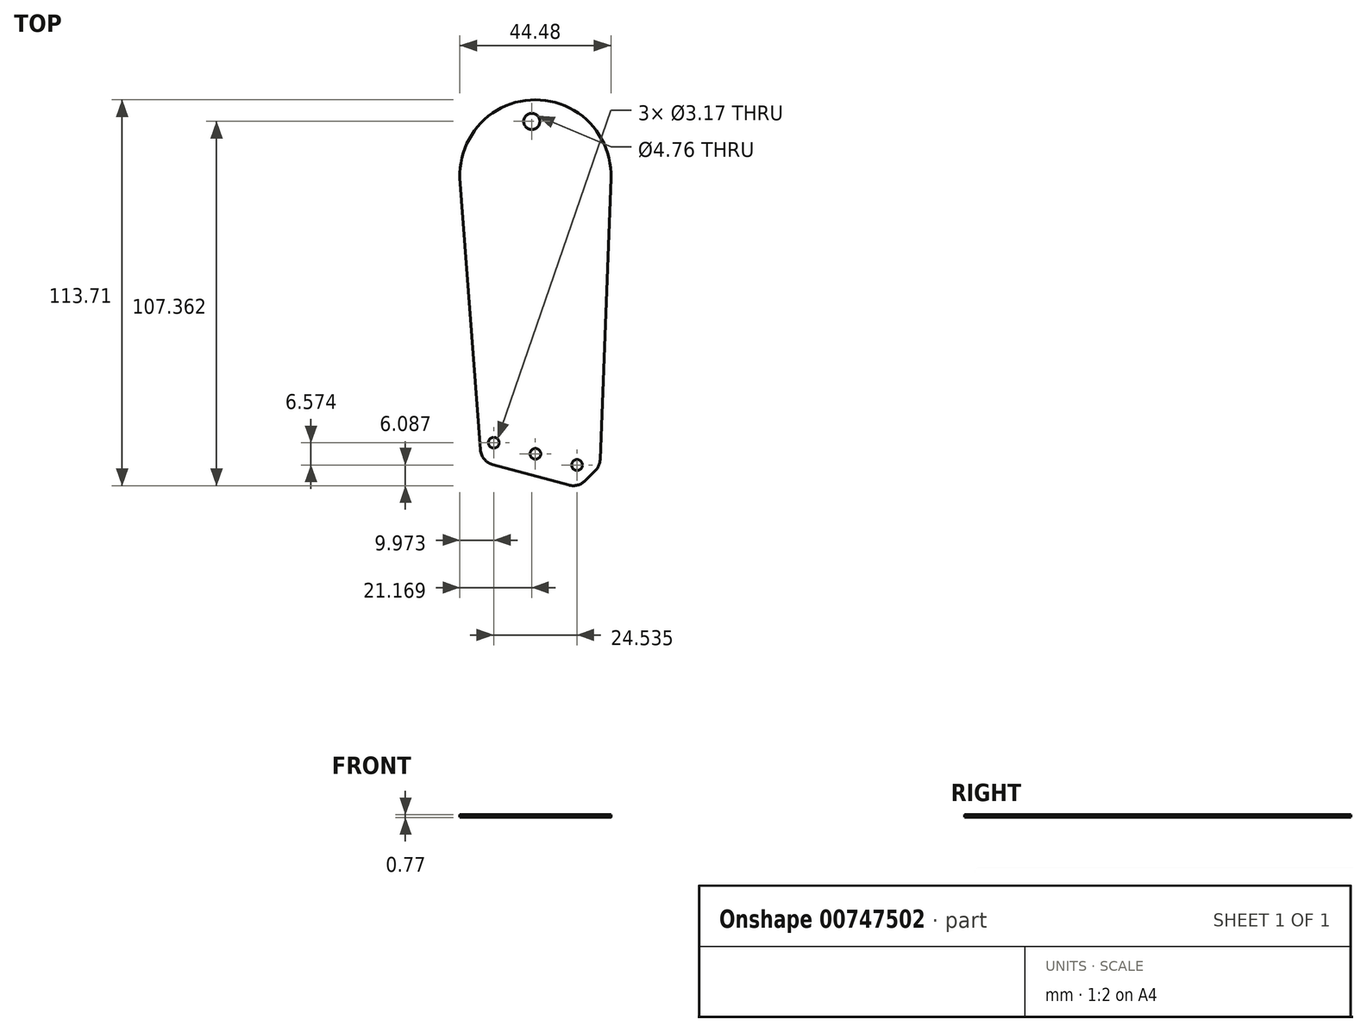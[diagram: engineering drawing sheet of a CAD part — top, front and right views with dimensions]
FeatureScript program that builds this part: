
annotation { "Feature Type Name" : "Feature", "Feature Type Description" : "" }
export const myFeature = defineFeature(function(context is Context, id is Id, definition is map)
    precondition{}
    {
        {
            var Q0;
            Q0=qCreatedBy(makeId("Right.planeOp"),FACE);
            var sketch = newSketch(context, id + "F0", { "sketchPlane" : qUnion([Q0])});
            skLineSegment(sketch, "E0", {"start": v(-73.39, -5.1) * mm, "end": v(-9.83, -5.1) * mm});
            skLineSegment(sketch, "E1", {"start": v(-9.83, -5.1) * mm, "end": v(40.91, -5.1) * mm});
            skPoint(sketch, "E2.visualSharp", {"position": v(-9.89, -5.1) * mm});
            skLineSegment(sketch, "E2.filletArc", {"start": v(-9.83, -5.1) * mm, "end": v(-9.83, -5.1) * mm});
            skLineSegment(sketch, "E3.0", {"start": v(-9.83, -5.87) * mm, "end": v(40.91, -5.87) * mm});
            skLineSegment(sketch, "E3.1", {"start": v(-9.83, -5.87) * mm, "end": v(-9.83, -5.87) * mm});
            skLineSegment(sketch, "E3.2", {"start": v(-73.39, -5.87) * mm, "end": v(-9.83, -5.87) * mm});
            skLineSegment(sketch, "E4", {"start": v(40.91, -5.87) * mm, "end": v(40.91, -5.1) * mm});
            skLineSegment(sketch, "E5", {"start": v(-73.39, -5.1) * mm, "end": v(-73.39, -5.87) * mm});
            skSolve(sketch);
        }
        {
            var Q0;
            Q0 = qSketchRegion(id + "F0", true);
            extrude(context, id + "F1", {"entities" : qUnion([Q0]), "endBound" : BoundingType.SYMMETRIC, "depth" : 101.6 * mm, "offsetDistance" : 25.4 * mm});
        }
        {
            var Q0;
            Q0=qCreatedBy(makeId("Top.planeOp"),FACE);
            var sketch = newSketch(context, id + "F2", { "sketchPlane" : qUnion([Q0])});
            skLineSegment(sketch, "E6", {"start": v(-20.03, 17.83) * mm, "end": v(-13.74, -65.73) * mm});
            skLineSegment(sketch, "E7", {"start": v(21.18, -67.04) * mm, "end": v(24.42, 17.83) * mm});
            skLineSegment(sketch, "E8", {"start": v(14.83, -73.39) * mm, "end": v(21.18, -67.04) * mm});
            skCircle(sketch, "E9", {"center": v(-10.5, -60.02) * mm, "radius": 1.59 * mm});
            skCircle(sketch, "E10", {"center": v(2.2, -63.43) * mm, "radius": 1.59 * mm});
            skCircle(sketch, "E11", {"center": v(14.9, -66.83) * mm, "radius": 1.59 * mm});
            skLineSegment(sketch, "E12.bottom", {"start": v(-71.62, 58.1) * mm, "end": v(69.87, 58.1) * mm});
            skLineSegment(sketch, "E12.top", {"start": v(-71.62, -139.59) * mm, "end": v(69.87, -139.59) * mm});
            skLineSegment(sketch, "E12.left", {"start": v(-71.62, 58.1) * mm, "end": v(-71.62, -139.59) * mm});
            skLineSegment(sketch, "E12.right", {"start": v(69.87, 58.1) * mm, "end": v(69.87, -139.59) * mm});
            skLineSegment(sketch, "E13", {"start": v(-10.5, -60.02) * mm, "end": v(14.9, -66.83) * mm});
            skLineSegment(sketch, "E14", {"start": v(-13.74, -65.73) * mm, "end": v(14.83, -73.39) * mm});
            skLineSegment(sketch, "E15", {"start": v(0.55, -69.56) * mm, "end": v(2.2, -63.43) * mm, "construction": true});
            skLineSegment(sketch, "E16", {"start": v(2.2, -63.43) * mm, "end": v(2.2, 18.67) * mm, "construction": true});
            skLineSegment(sketch, "E17", {"start": v(-20.03, 17.83) * mm, "end": v(24.42, 17.83) * mm, "construction": true});
            skArc(sketch, "E18", {"start": v(24.42, 17.83) * mm, "mid": v(2.2, 40.91) * mm, "end": v(-20.03, 17.83) * mm});
            skSolve(sketch);
        }
        {
            var Q0;
            Q0 = qSketchRegion(id + "F2", true);
            extrude(context, id + "F3", {"entities" : qUnion([Q0]), "operationType" : NewBodyOperationType.REMOVE, "oppositeDirection" : true, "depth" : 25.4 * mm, "offsetDistance" : 25.4 * mm});
        }
        {
            var Q0;
            Q0=makeQuery(id+"F1.opExtrude","SWEPT_FACE",FACE,{"disambiguationData":[OSD([sQuery(id+"F0.wireOp",EDGE,"E0")])]});
            var sketch = newSketch(context, id + "F4", { "sketchPlane" : qUnion([Q0])});
            skCircle(sketch, "E19", {"center": v(-10.08, -60.14) * mm, "radius": 1.59 * mm});
            skCircle(sketch, "E20", {"center": v(2.2, -63.43) * mm, "radius": 1.59 * mm});
            skCircle(sketch, "E21", {"center": v(14.46, -66.71) * mm, "radius": 1.59 * mm});
            skLineSegment(sketch, "E22", {"start": v(-10.08, -60.14) * mm, "end": v(14.46, -66.71) * mm, "construction": true});
            skLineSegment(sketch, "E23", {"start": v(2.2, -63.43) * mm, "end": v(0.55, -69.56) * mm, "construction": true});
            skSolve(sketch);
        }
        {
            var Q0;
            Q0 = qSketchRegion(id + "F4", true);
            extrude(context, id + "F5", {"entities" : qUnion([Q0]), "operationType" : NewBodyOperationType.REMOVE, "oppositeDirection" : true, "depth" : 25.4 * mm, "offsetDistance" : 25.4 * mm});
        }
        {
            var Q0;
            Q0=makeQuery(id+"F1.opExtrude","SWEPT_FACE",FACE,{"disambiguationData":[OSD([sQuery(id+"F0.wireOp",EDGE,"E1")])]});
            var sketch = newSketch(context, id + "F6", { "sketchPlane" : qUnion([Q0])});
            skLineSegment(sketch, "E24", {"start": v(1.12, 40.91) * mm, "end": v(1.12, 19.82) * mm, "construction": true});
            skCircle(sketch, "E25", {"center": v(1.12, 34.56) * mm, "radius": 2.38 * mm});
            skSolve(sketch);
        }
        {
            var Q0;
            Q0 = qSketchRegion(id + "F6", true);
            extrude(context, id + "F7", {"entities" : qUnion([Q0]), "operationType" : NewBodyOperationType.REMOVE, "oppositeDirection" : true, "depth" : 25.4 * mm, "offsetDistance" : 25.4 * mm});
        }
        {
            var Q0;
            Q0=makeQuery(id+"F3.boolean.opBoolean","COPY",EDGE,{"derivedFrom":makeQuery(id+"F3.opExtrude","SWEPT_EDGE",EDGE,{"disambiguationData":[OSD([sQuery(id+"F2.wireOp",EDGE,"E6"),sQuery(id+"F2.wireOp",EDGE,"E14")])]})});
            var Q1;
            Q1=makeQuery(id+"F3.boolean.opBoolean","COPY",EDGE,{"derivedFrom":makeQuery(id+"F3.opExtrude","SWEPT_EDGE",EDGE,{"disambiguationData":[OSD([sQuery(id+"F2.wireOp",EDGE,"E8"),sQuery(id+"F2.wireOp",EDGE,"E14")])]})});
            var Q2;
            Q2=makeQuery(id+"F3.boolean.opBoolean","COPY",EDGE,{"derivedFrom":makeQuery(id+"F3.opExtrude","SWEPT_EDGE",EDGE,{"disambiguationData":[OSD([sQuery(id+"F2.wireOp",EDGE,"E7"),sQuery(id+"F2.wireOp",EDGE,"E8")])]})});
            fillet(context, id + "F8", {"entities" : qUnion([Q0, Q1, Q2]), "radius" : 5.08 * mm, "tangentPropagation" : true, "allowEdgeOverflow" : false});
        }
    });
